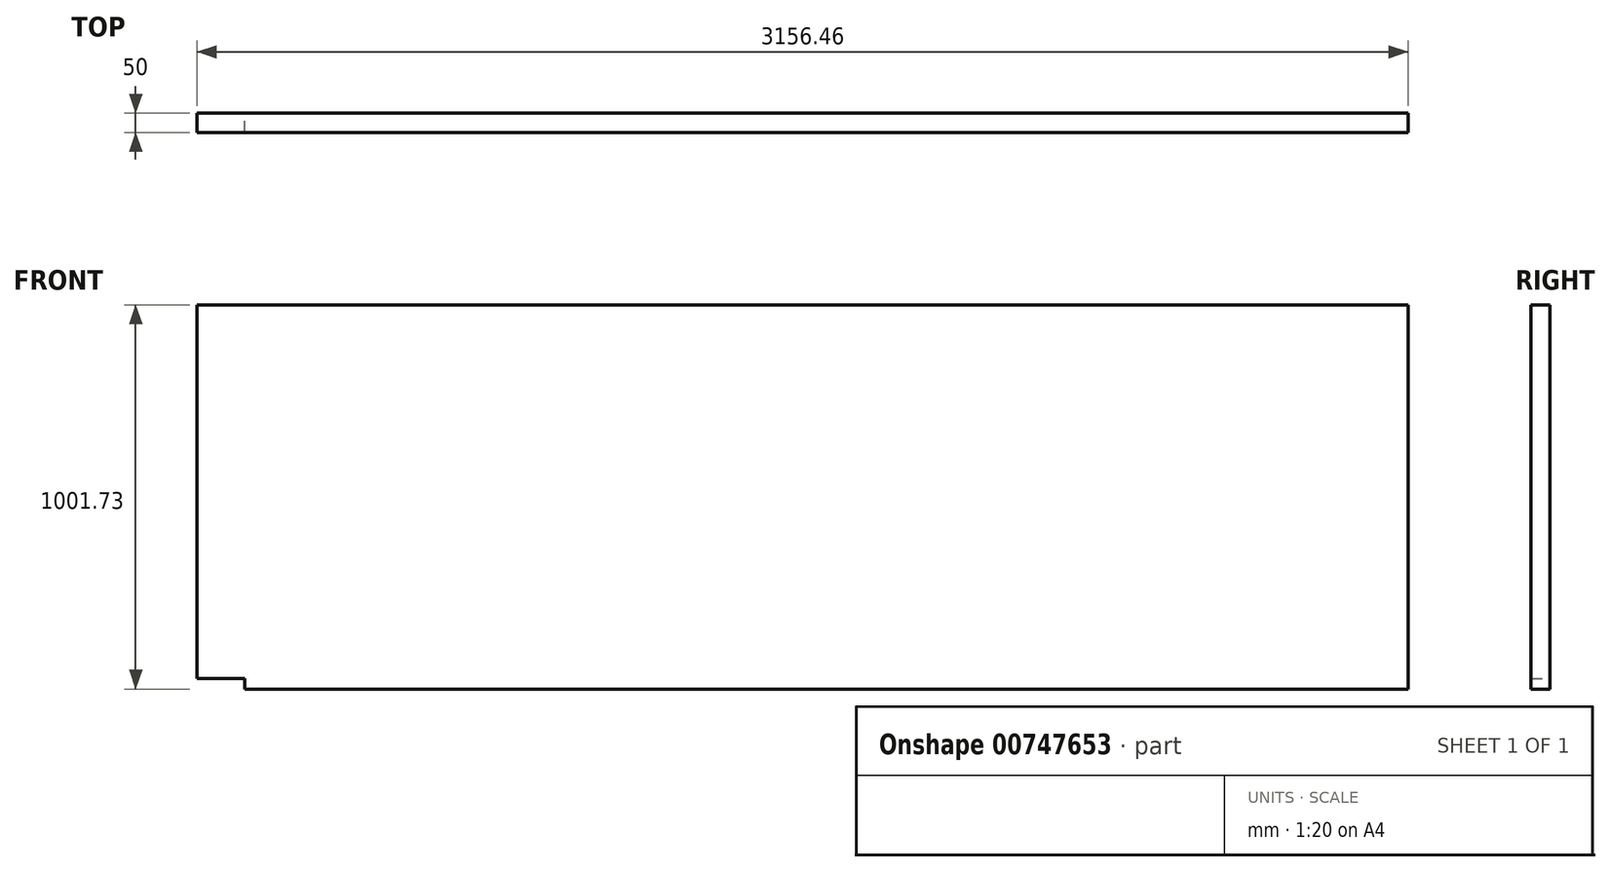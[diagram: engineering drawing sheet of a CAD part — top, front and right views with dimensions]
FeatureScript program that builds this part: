
annotation { "Feature Type Name" : "Feature", "Feature Type Description" : "" }
export const myFeature = defineFeature(function(context is Context, id is Id, definition is map)
    precondition{}
    {
        {
            var Q0;
            Q0=qCreatedBy(makeId("Front.planeOp"),FACE);
            var sketch = newSketch(context, id + "F0", { "sketchPlane" : qUnion([Q0])});
            skLineSegment(sketch, "E0.top", {"start": v(-1115.45, -552.71) * mm, "end": v(1917.05, -552.71) * mm});
            skLineSegment(sketch, "E0.right", {"start": v(1917.05, 449.02) * mm, "end": v(1917.05, -552.71) * mm});
            skLineSegment(sketch, "E1.top", {"start": v(-1115.45, -525.04) * mm, "end": v(-1239.41, -525.04) * mm});
            skLineSegment(sketch, "E1.left", {"start": v(-1115.45, -552.71) * mm, "end": v(-1115.45, -525.04) * mm});
            skLineSegment(sketch, "E2", {"start": v(-1239.41, -525.04) * mm, "end": v(-1239.41, 449.02) * mm});
            skLineSegment(sketch, "E3", {"start": v(-1239.41, 449.02) * mm, "end": v(1917.05, 449.02) * mm});
            skSolve(sketch);
        }
        {
            var Q0;
            Q0=makeQuery(id+"F0.imprint","IMPRINT",FACE,{"disambiguationData":[TD([[makeQuery(id+"F0.imprint","IMPRINT",EDGE,{"derivedFrom":sQuery(id+"F0.wireOp",EDGE,"E0.top")}),1.0]])]});
            extrude(context, id + "F1", {"entities" : qUnion([Q0]), "endBound" : BoundingType.SYMMETRIC, "depth" : 50 * mm, "offsetDistance" : 25 * mm});
        }
    });
